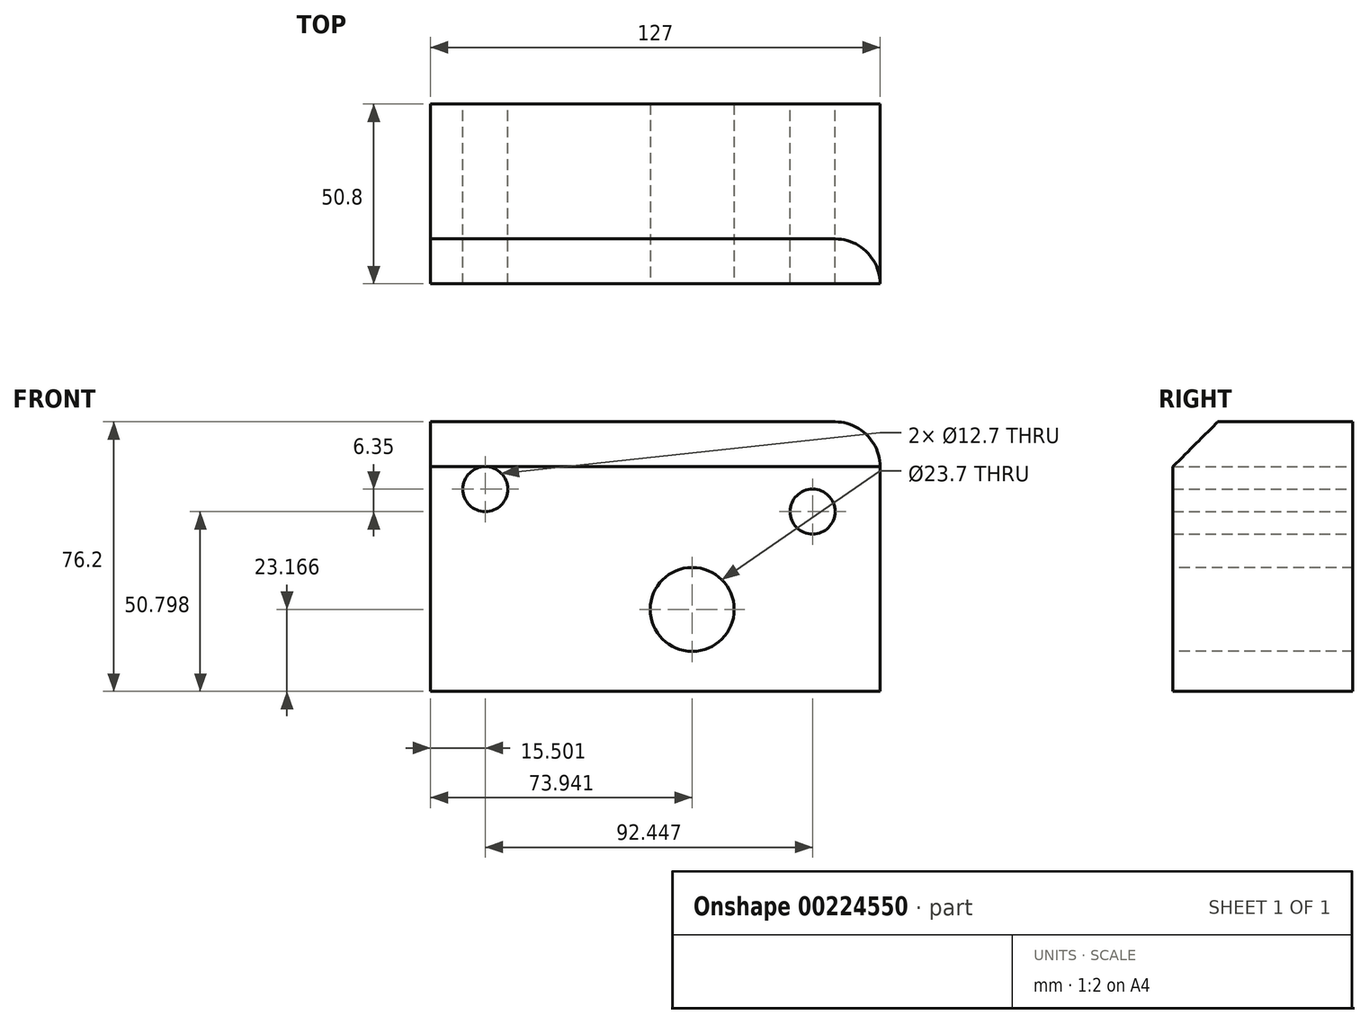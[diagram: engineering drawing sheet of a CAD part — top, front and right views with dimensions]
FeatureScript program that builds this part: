
annotation { "Feature Type Name" : "Feature", "Feature Type Description" : "" }
export const myFeature = defineFeature(function(context is Context, id is Id, definition is map)
    precondition{}
    {
        {
            var Q0;
            Q0=qCreatedBy(makeId("Front.planeOp"),FACE);
            var sketch = newSketch(context, id + "F0", { "sketchPlane" : qUnion([Q0])});
            skLineSegment(sketch, "E0.bottom", {"start": v(-52.95, 32.7) * mm, "end": v(74.05, 32.7) * mm});
            skLineSegment(sketch, "E0.top", {"start": v(-52.95, -43.5) * mm, "end": v(74.05, -43.5) * mm});
            skLineSegment(sketch, "E0.left", {"start": v(-52.95, 32.7) * mm, "end": v(-52.95, -43.5) * mm});
            skLineSegment(sketch, "E0.right", {"start": v(74.05, 32.7) * mm, "end": v(74.05, -43.5) * mm});
            skCircle(sketch, "E1", {"center": v(55, 7.3) * mm, "radius": 6.35 * mm});
            skCircle(sketch, "E2", {"center": v(-37.45, 13.66) * mm, "radius": 6.35 * mm});
            skSolve(sketch);
        }
        {
            var Q0;
            Q0=makeQuery(id+"F0.imprint","IMPRINT",FACE,{"disambiguationData":[TD([[makeQuery(id+"F0.imprint","IMPRINT",EDGE,{"derivedFrom":sQuery(id+"F0.wireOp",EDGE,"E0.bottom")}),-1.0]])]});
            extrude(context, id + "F1", {"entities" : qUnion([Q0]), "depth" : 50.8 * mm});
        }
        {
            var Q0;
            Q0=makeQuery(id+"F1.opExtrude","CAP_FACE",FACE,{"disambiguationData":[OSD([sQuery(id+"F0.wireOp",EDGE,"E0.bottom"),sQuery(id+"F0.wireOp",EDGE,"E0.top"),sQuery(id+"F0.wireOp",EDGE,"E0.left"),sQuery(id+"F0.wireOp",EDGE,"E0.right"),sQuery(id+"F0.wireOp",EDGE,"E1"),sQuery(id+"F0.wireOp",EDGE,"E2")])],"isStart":false});
            var sketch = newSketch(context, id + "F2", { "sketchPlane" : qUnion([Q0])});
            skCircle(sketch, "E3", {"center": v(21, -20.32) * mm, "radius": 11.85 * mm});
            skSolve(sketch);
        }
        {
            var Q0;
            Q0 = qSketchRegion(id + "F2", true);
            extrude(context, id + "F3", {"entities" : qUnion([Q0]), "operationType" : NewBodyOperationType.REMOVE, "oppositeDirection" : true, "depth" : 71.63 * mm});
        }
        {
            var Q0;
            Q0=makeQuery(id+"F1.opExtrude","CAP_EDGE",EDGE,{"disambiguationData":[OSD([sQuery(id+"F0.wireOp",EDGE,"E0.bottom")])],"isStart":false});
            chamfer(context, id + "F4", {"entities" : qUnion([Q0]), "width" : 12.7 * mm, "tangentPropagation" : true});
        }
        {
            var Q0;
            Q0=makeQuery(id+"F1.opExtrude","SWEPT_EDGE",EDGE,{"disambiguationData":[OSD([sQuery(id+"F0.wireOp",EDGE,"E0.bottom"),sQuery(id+"F0.wireOp",EDGE,"E0.right")])]});
            fillet(context, id + "F5", {"entities" : qUnion([Q0]), "radius" : 12.7 * mm, "tangentPropagation" : true, "allowEdgeOverflow" : false});
        }
    });
